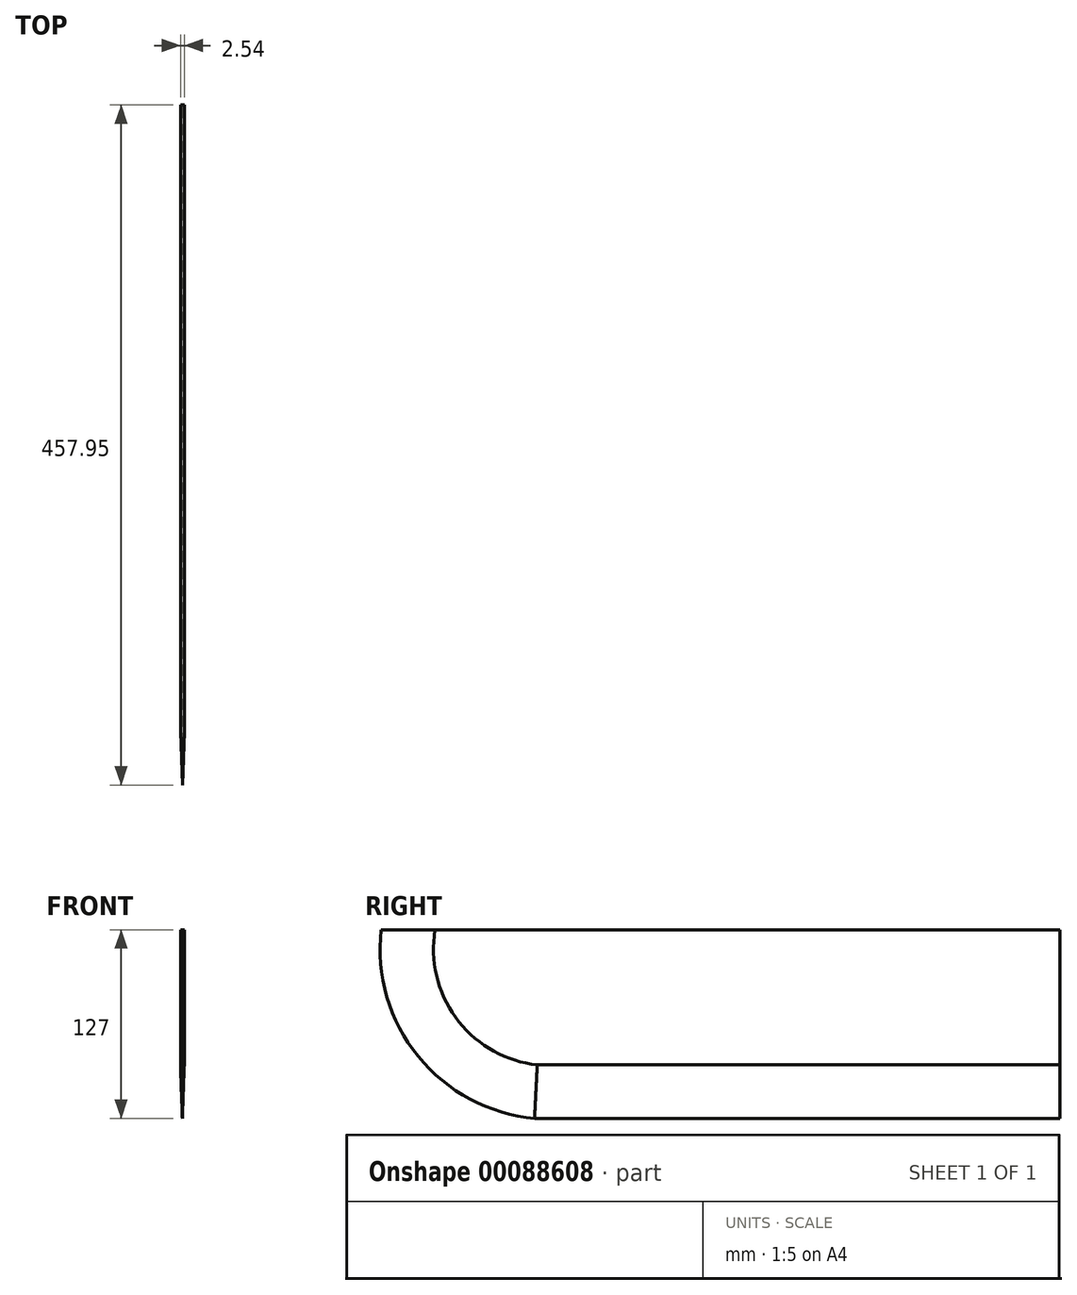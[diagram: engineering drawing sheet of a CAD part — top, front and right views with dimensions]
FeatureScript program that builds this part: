
annotation { "Feature Type Name" : "Feature", "Feature Type Description" : "" }
export const myFeature = defineFeature(function(context is Context, id is Id, definition is map)
    precondition{}
    {
        {
            var Q0;
            Q0=qCreatedBy(makeId("Right.planeOp"),FACE);
            var sketch = newSketch(context, id + "F0", { "sketchPlane" : qUnion([Q0])});
            skLineSegment(sketch, "E0", {"start": v(0, 0) * mm, "end": v(457.2, 0) * mm});
            skLineSegment(sketch, "E1", {"start": v(103.33, -127) * mm, "end": v(457.2, -127) * mm});
            skLineSegment(sketch, "E2", {"start": v(457.2, 0) * mm, "end": v(457.2, -127) * mm});
            skArc(sketch, "E3", {"start": v(0, 0) * mm, "mid": v(24.9, -85.28) * mm, "end": v(103.33, -127) * mm});
            skSolve(sketch);
        }
        {
            var Q0;
            Q0 = qSketchRegion(id + "F0", true);
            extrude(context, id + "F1", {"entities" : qUnion([Q0]), "depth" : 2.54 * mm});
        }
        {
            var Q0;
            Q0=makeQuery(id+"F1.opExtrude","SWEPT_FACE",FACE,{"disambiguationData":[OSD([sQuery(id+"F0.wireOp",EDGE,"E2")])]});
            var sketch = newSketch(context, id + "F2", { "sketchPlane" : qUnion([Q0])});
            skLineSegment(sketch, "E4", {"start": v(-2.54, -91.03) * mm, "end": v(-1.27, -127) * mm});
            skLineSegment(sketch, "E5", {"start": v(0, -91.03) * mm, "end": v(-1.27, -127) * mm});
            skSolve(sketch);
        }
        {
            var Q0;
            Q0 = qSketchRegion(id + "F2", true);
            var Q1;
            {var subQ0=sQuery(id+"F2.wireOp",EDGE,"E4");Q1=makeQuery(id+"F2.imprint","IMPRINT",FACE,{"disambiguationData":[TD([[makeQuery(id+"F2.imprint","IMPRINT",EDGE,{"derivedFrom":subQ0}),-1.0]])]});}
            var Q2;
            {var subQ0=sQuery(id+"F2.wireOp",EDGE,"E5");Q2=makeQuery(id+"F2.imprint","IMPRINT",FACE,{"disambiguationData":[TD([[makeQuery(id+"F2.imprint","IMPRINT",EDGE,{"derivedFrom":subQ0}),1.0]])]});}
            extrude(context, id + "F3", {"entities" : qUnion([Q0, Q1, Q2]), "operationType" : NewBodyOperationType.REMOVE, "oppositeDirection" : true, "depth" : 25.4 * mm});
        }
        {
            var Q0;
            Q0=makeQuery(id+"F3.boolean.opBoolean","COPY",FACE,{"derivedFrom":makeQuery(id+"F3.opExtrude","CAP_FACE",FACE,{"disambiguationData":[OSD([sQuery(id+"F0.wireOp",EDGE,"E1"),sQuery(id+"F0.wireOp",EDGE,"E2"),sQuery(id+"F2.wireOp",EDGE,"E4")])],"isStart":false})});
            var Q1;
            Q1=makeQuery(id+"F3.boolean.opBoolean","COPY",FACE,{"derivedFrom":makeQuery(id+"F3.opExtrude","CAP_FACE",FACE,{"disambiguationData":[OSD([sQuery(id+"F0.wireOp",EDGE,"E1"),sQuery(id+"F0.wireOp",EDGE,"E2"),sQuery(id+"F2.wireOp",EDGE,"E5")])],"isStart":false})});
            var Q2;
            Q2=makeQuery(id+"F1.opExtrude","CAP_EDGE",EDGE,{"disambiguationData":[OSD([sQuery(id+"F0.wireOp",EDGE,"E1")])],"isStart":false});
            var Q3;
            Q3=makeQuery(id+"F1.opExtrude","CAP_EDGE",EDGE,{"disambiguationData":[OSD([sQuery(id+"F0.wireOp",EDGE,"E3")])],"isStart":false});
            sweep(context, id + "F4", {"operationType" : NewBodyOperationType.REMOVE, "profiles" : qUnion([Q0, Q1]), "path" : qUnion([Q2, Q3])});
        }
        {
            var Q0;
            Q0=makeQuery(id+"F4.boolean.opBoolean","COPY",FACE,{"derivedFrom":makeQuery(id+"F4.opSweep","CAP_FACE",FACE,{"disambiguationData":[OSD([sQuery(id+"F0.wireOp",EDGE,"E0"),sQuery(id+"F0.wireOp",EDGE,"E1"),sQuery(id+"F0.wireOp",EDGE,"E2"),sQuery(id+"F0.wireOp",EDGE,"E3"),sQuery(id+"F2.wireOp",EDGE,"E4")])],"isStart":false})});
            var Q1;
            Q1=makeQuery(id+"F4.boolean.opBoolean","COPY",FACE,{"derivedFrom":makeQuery(id+"F4.opSweep","CAP_FACE",FACE,{"disambiguationData":[OSD([sQuery(id+"F0.wireOp",EDGE,"E0"),sQuery(id+"F0.wireOp",EDGE,"E1"),sQuery(id+"F0.wireOp",EDGE,"E2"),sQuery(id+"F0.wireOp",EDGE,"E3"),sQuery(id+"F2.wireOp",EDGE,"E5")])],"isStart":false})});
            extrude(context, id + "F5", {"entities" : qUnion([Q0, Q1]), "operationType" : NewBodyOperationType.REMOVE, "oppositeDirection" : true, "depth" : 25.4 * mm});
        }
    });
